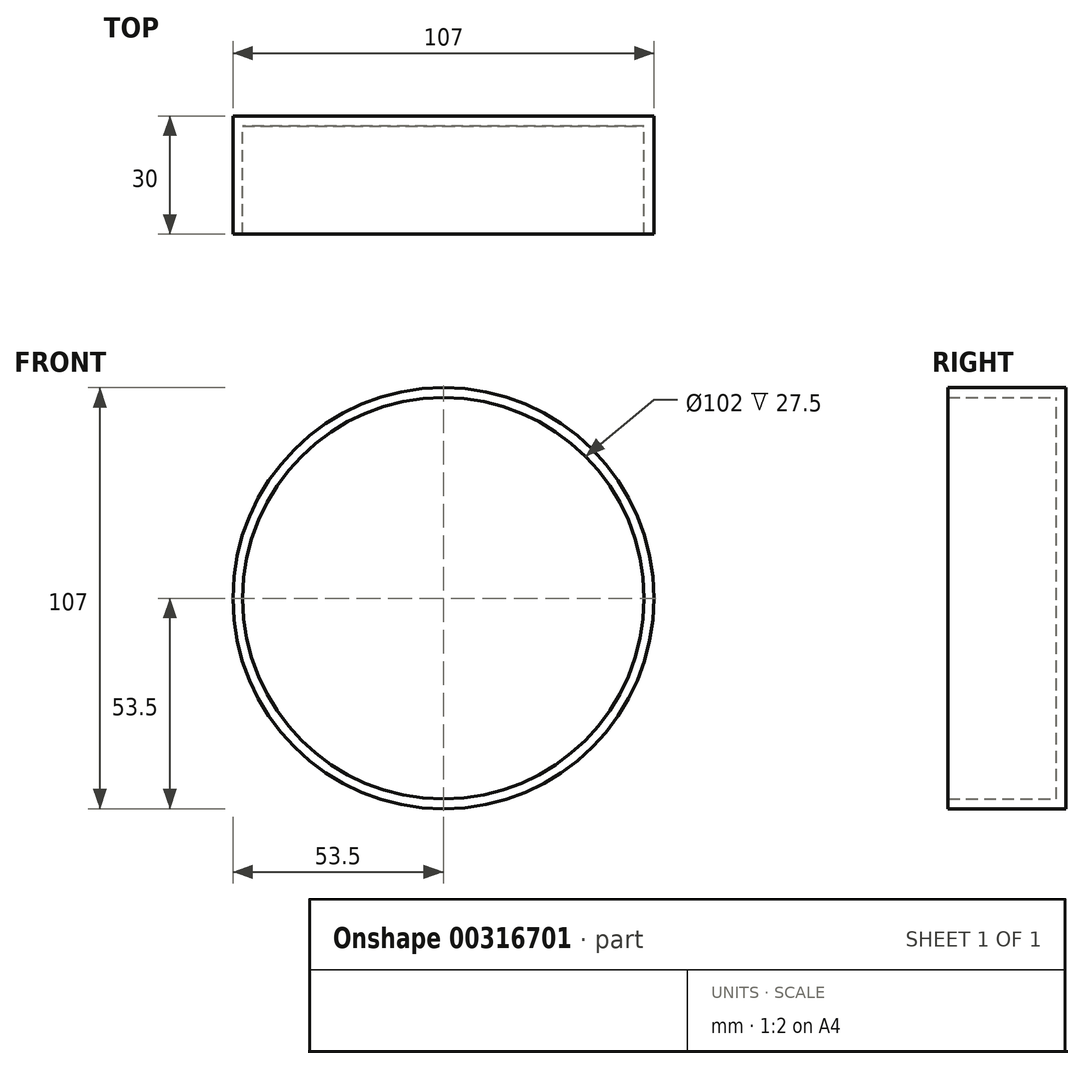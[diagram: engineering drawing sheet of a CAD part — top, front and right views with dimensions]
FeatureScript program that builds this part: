
annotation { "Feature Type Name" : "Feature", "Feature Type Description" : "" }
export const myFeature = defineFeature(function(context is Context, id is Id, definition is map)
    precondition{}
    {
        {
            var Q0;
            Q0=qCreatedBy(makeId("Front.planeOp"),FACE);
            var sketch = newSketch(context, id + "F0", { "sketchPlane" : qUnion([Q0])});
            skCircle(sketch, "E0", {"center": v(0, 0) * mm, "radius": 51.5 * mm});
            skCircle(sketch, "E1", {"center": v(0, 0) * mm, "radius": 53.5 * mm});
            skSolve(sketch);
        }
        {
            var Q0;
            Q0=makeQuery(id+"F0.imprint","IMPRINT",FACE,{"disambiguationData":[TD([[makeQuery(id+"F0.imprint","IMPRINT",EDGE,{"derivedFrom":sQuery(id+"F0.wireOp",EDGE,"E0")}),1.0]])]});
            var Q1;
            Q1=makeQuery(id+"F0.imprint","IMPRINT",FACE,{"disambiguationData":[TD([[makeQuery(id+"F0.imprint","IMPRINT",EDGE,{"derivedFrom":sQuery(id+"F0.wireOp",EDGE,"E0")}),-1.0]])]});
            extrude(context, id + "F1", {"entities" : qUnion([Q0, Q1]), "depth" : 30 * mm});
        }
        {
            var Q0;
            Q0=makeQuery(id+"F1.opExtrude","CAP_FACE",FACE,{"disambiguationData":[OSD([sQuery(id+"F0.wireOp",EDGE,"E1")])],"isStart":false});
            shell(context, id + "F2", {"entities" : qUnion([Q0]), "thickness" : 2.5 * mm});
        }
    });
